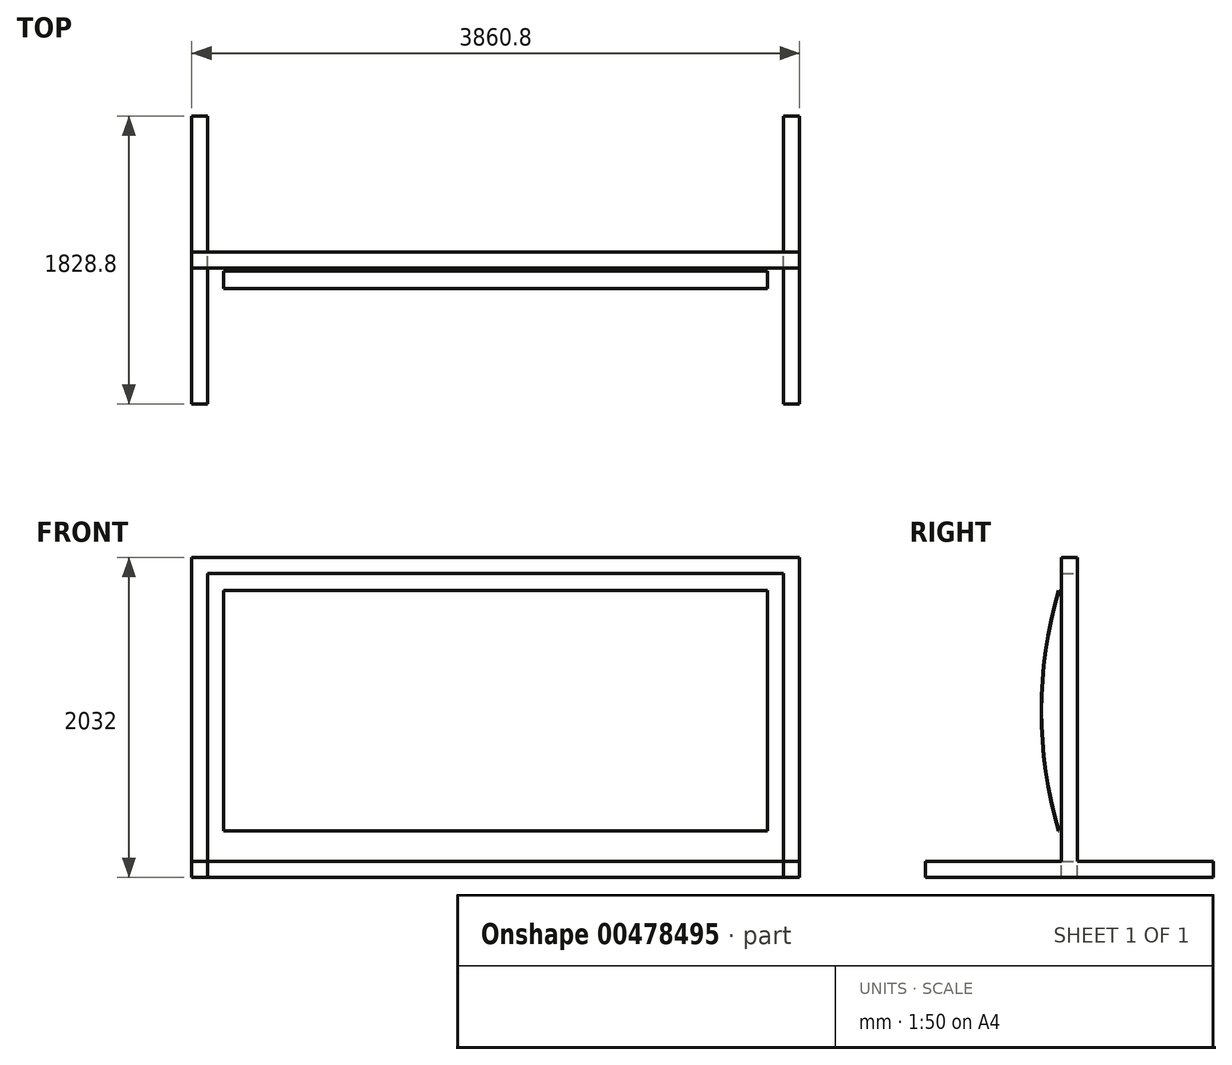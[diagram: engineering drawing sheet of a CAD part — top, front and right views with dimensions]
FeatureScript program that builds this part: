
annotation { "Feature Type Name" : "Feature", "Feature Type Description" : "" }
export const myFeature = defineFeature(function(context is Context, id is Id, definition is map)
    precondition{}
    {
        {
            var Q0;
            Q0=qCreatedBy(makeId("Front.planeOp"),FACE);
            var sketch = newSketch(context, id + "F0", { "sketchPlane" : qUnion([Q0])});
            skLineSegment(sketch, "E0", {"start": v(0, 0) * mm, "end": v(0, 101.6) * mm});
            skLineSegment(sketch, "E1", {"start": v(0, 101.6) * mm, "end": v(1828.8, 101.6) * mm});
            skLineSegment(sketch, "E2", {"start": v(1828.8, 101.6) * mm, "end": v(1828.8, 1930.4) * mm});
            skLineSegment(sketch, "E3", {"start": v(1828.8, 1930.4) * mm, "end": v(0, 1930.4) * mm});
            skLineSegment(sketch, "E4", {"start": v(0, 1930.4) * mm, "end": v(0, 2032) * mm});
            skLineSegment(sketch, "E5", {"start": v(0, 2032) * mm, "end": v(1930.4, 2032) * mm});
            skLineSegment(sketch, "E6", {"start": v(1930.4, 2032) * mm, "end": v(1930.4, 0) * mm});
            skLineSegment(sketch, "E7", {"start": v(1930.4, 0) * mm, "end": v(0, 0) * mm});
            skLineSegment(sketch, "E8.MirrorCS", {"start": v(0, 101.6) * mm, "end": v(-1828.8, 101.6) * mm});
            skLineSegment(sketch, "E9.MirrorCS", {"start": v(0, 2032) * mm, "end": v(-1930.4, 2032) * mm});
            skLineSegment(sketch, "E10.MirrorCS", {"start": v(-1930.4, 0) * mm, "end": v(0, 0) * mm});
            skLineSegment(sketch, "E11.MirrorCS", {"start": v(-1828.8, 101.6) * mm, "end": v(-1828.8, 1930.4) * mm});
            skLineSegment(sketch, "E12.MirrorCS", {"start": v(-1828.8, 1930.4) * mm, "end": v(0, 1930.4) * mm});
            skLineSegment(sketch, "E13.MirrorCS", {"start": v(-1930.4, 2032) * mm, "end": v(-1930.4, 0) * mm});
            skSolve(sketch);
        }
        {
            var Q0;
            Q0 = qSketchRegion(id + "F0", true);
            extrude(context, id + "F1", {"entities" : qUnion([Q0]), "depth" : 50.8 * mm, "hasSecondDirection" : true, "secondDirectionOppositeDirection" : true, "secondDirectionDepth" : 50.8 * mm});
        }
        {
            var Q0;
            Q0=qCreatedBy(makeId("Front.planeOp"),FACE);
            var sketch = newSketch(context, id + "F2", { "sketchPlane" : qUnion([Q0])});
            skLineSegment(sketch, "E14.bottom", {"start": v(1828.8, 101.6) * mm, "end": v(1930.4, 101.6) * mm});
            skLineSegment(sketch, "E14.top", {"start": v(1828.8, 0) * mm, "end": v(1930.4, 0) * mm});
            skLineSegment(sketch, "E14.left", {"start": v(1828.8, 101.6) * mm, "end": v(1828.8, 0) * mm});
            skLineSegment(sketch, "E14.right", {"start": v(1930.4, 101.6) * mm, "end": v(1930.4, 0) * mm});
            skLineSegment(sketch, "E15.MirrorCS", {"start": v(-1930.4, 101.6) * mm, "end": v(-1930.4, 0) * mm});
            skLineSegment(sketch, "E16.MirrorCS", {"start": v(-1828.8, 101.6) * mm, "end": v(-1828.8, 0) * mm});
            skLineSegment(sketch, "E17.MirrorCS", {"start": v(-1828.8, 101.6) * mm, "end": v(-1930.4, 101.6) * mm});
            skLineSegment(sketch, "E18.MirrorCS", {"start": v(-1828.8, 0) * mm, "end": v(-1930.4, 0) * mm});
            skSolve(sketch);
        }
        {
            var Q0;
            Q0 = qSketchRegion(id + "F2", true);
            extrude(context, id + "F3", {"entities" : qUnion([Q0]), "operationType" : NewBodyOperationType.ADD, "depth" : 914.4 * mm, "hasSecondDirection" : true, "secondDirectionOppositeDirection" : true, "secondDirectionDepth" : 914.4 * mm});
        }
        {
            var Q0;
            Q0=qCreatedBy(makeId("Right.planeOp"),FACE);
            var sketch = newSketch(context, id + "F4", { "sketchPlane" : qUnion([Q0])});
            skArc(sketch, "E19", {"start": v(-68.82, 1820.6) * mm, "mid": v(-178.07, 1058.6) * mm, "end": v(-68.82, 296.6) * mm});
            skLineSegment(sketch, "E20", {"start": v(-68.82, 1820.6) * mm, "end": v(-68.82, 296.6) * mm, "construction": true});
            skArc(sketch, "E21", {"start": v(-71.02, 1821.23) * mm, "mid": v(-180.35, 1058.6) * mm, "end": v(-71.02, 295.95) * mm});
            skLineSegment(sketch, "E22", {"start": v(-71.02, 295.95) * mm, "end": v(2534.1, 1058.6) * mm, "construction": true});
            skLineSegment(sketch, "E23", {"start": v(2534.1, 1058.6) * mm, "end": v(-71.02, 1821.23) * mm, "construction": true});
            skLineSegment(sketch, "E24", {"start": v(-71.02, 1821.23) * mm, "end": v(-68.82, 1820.6) * mm});
            skLineSegment(sketch, "E25", {"start": v(-71.02, 295.95) * mm, "end": v(-68.82, 296.6) * mm});
            skSolve(sketch);
        }
        {
            var Q0;
            Q0 = qSketchRegion(id + "F4", true);
            extrude(context, id + "F5", {"entities" : qUnion([Q0]), "depth" : 1727.2 * mm, "hasSecondDirection" : true, "secondDirectionOppositeDirection" : true, "secondDirectionDepth" : 1727.2 * mm});
        }
    });
